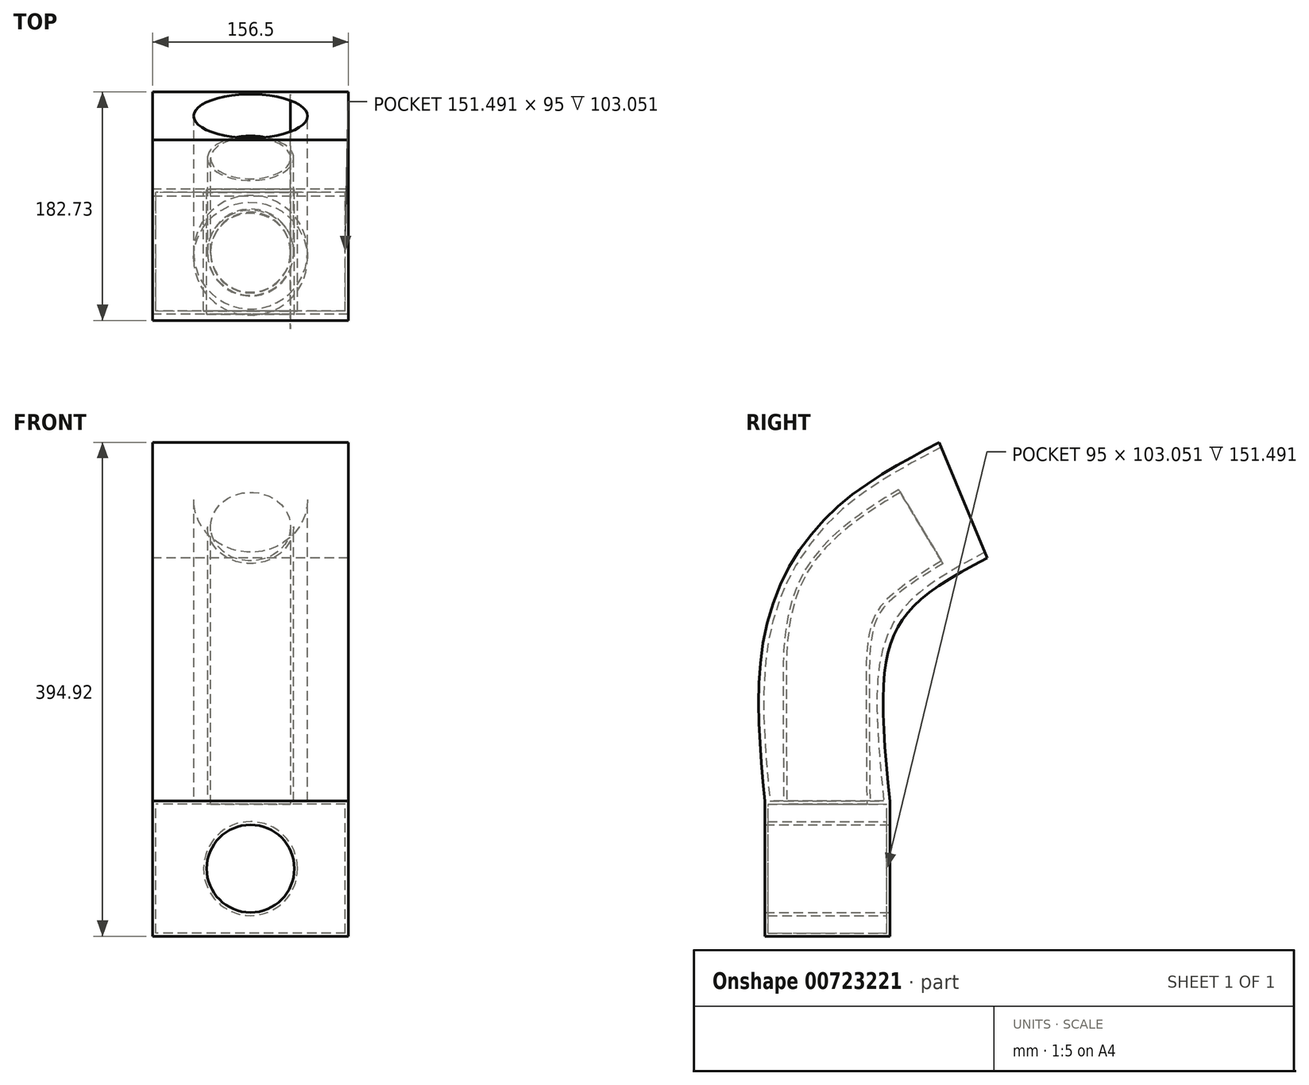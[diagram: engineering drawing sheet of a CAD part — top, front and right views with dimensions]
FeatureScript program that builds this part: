
annotation { "Feature Type Name" : "Feature", "Feature Type Description" : "" }
export const myFeature = defineFeature(function(context is Context, id is Id, definition is map)
    precondition{}
    {
        {
            var Q0;
            Q0=qCreatedBy(makeId("Front.planeOp"),FACE);
            var sketch = newSketch(context, id + "F0", { "sketchPlane" : qUnion([Q0])});
            skLineSegment(sketch, "E0.bottom", {"start": v(78.25, -54.03) * mm, "end": v(-78.25, -54.03) * mm});
            skLineSegment(sketch, "E0.top", {"start": v(78.25, 54.03) * mm, "end": v(-78.25, 54.03) * mm});
            skLineSegment(sketch, "E0.left", {"start": v(78.25, -54.03) * mm, "end": v(78.25, 54.03) * mm});
            skLineSegment(sketch, "E0.right", {"start": v(-78.25, -54.03) * mm, "end": v(-78.25, 54.03) * mm});
            skPoint(sketch, "E0.middle", {"position": v(0, 0) * mm});
            skCircle(sketch, "E1", {"center": v(0, 0) * mm, "radius": 35.05 * mm});
            skSolve(sketch);
        }
        {
            var Q0;
            Q0 = qSketchRegion(id + "F0", true);
            extrude(context, id + "F1", {"entities" : qUnion([Q0]), "depth" : 100 * mm, "offsetDistance" : 25 * mm});
        }
        {
            var Q0;
            Q0=qCreatedBy(makeId("Right.planeOp"),FACE);
            var sketch = newSketch(context, id + "F2", { "sketchPlane" : qUnion([Q0])});
            skFitSpline(sketch, "E2", {"points": [v(-49.93, 54.4) * mm, v(-50.5, 144.15) * mm, v(-38.34, 219.97) * mm, v(25.3, 273.32) * mm], "startDerivative": vector(-2.27, 260.13) * mm, "endDerivative": vector(229.88, 140.85) * mm});
            skSolve(sketch);
        }
        {
            var Q0;
            Q0=makeQuery(id+"F1.opExtrude","SWEPT_FACE",FACE,{"disambiguationData":[OSD([sQuery(id+"F0.wireOp",EDGE,"E0.top")])]});
            var sketch = newSketch(context, id + "F3", { "sketchPlane" : qUnion([Q0])});
            skCircle(sketch, "E3", {"center": v(0, -50.42) * mm, "radius": 34.47 * mm});
            skSolve(sketch);
        }
        {
            var Q0;
            Q0=makeQuery(id+"F3.imprint","IMPRINT",FACE,{"disambiguationData":[TD([[makeQuery(id+"F3.imprint","IMPRINT",EDGE,{"derivedFrom":sQuery(id+"F3.wireOp",EDGE,"E3")}),1.0]])]});
            var Q1;
            Q1=sQuery(id+"F2.wireOp",EDGE,"E2");
            sweep(context, id + "F4", {"operationType" : NewBodyOperationType.ADD, "profiles" : qUnion([Q0]), "path" : qUnion([Q1])});
        }
        {
            var Q0;
            Q0=makeQuery(id+"F4.opSweep","CAP_FACE",FACE,{"disambiguationData":[OSD([sQuery(id+"F2.wireOp",VERTEX,"E2.end"),sQuery(id+"F3.wireOp",EDGE,"E3")])],"isStart":false});
            shell(context, id + "F5", {"entities" : qUnion([Q0]), "thickness" : 2.5 * mm});
        }
        {
            var Q0;
            Q0=makeQuery(id+"F1.opExtrude","SWEPT_FACE",FACE,{"disambiguationData":[OSD([sQuery(id+"F0.wireOp",EDGE,"E0.top")])]});
            var sketch = newSketch(context, id + "F6", { "sketchPlane" : qUnion([Q0])});
            skCircle(sketch, "E4", {"center": v(0, -50.42) * mm, "radius": 45.5 * mm});
            skSolve(sketch);
        }
        {
            var Q0;
            Q0=qCreatedBy(makeId("Right.planeOp"),FACE);
            var sketch = newSketch(context, id + "F7", { "sketchPlane" : qUnion([Q0])});
            skFitSpline(sketch, "E5", {"points": [v(-50.92, 53.77) * mm, v(-52.32, 177.4) * mm, v(-14.2, 248.3) * mm, v(58.24, 295.57) * mm], "startDerivative": vector(-33.85, 348.5) * mm, "endDerivative": vector(249.2, 132.76) * mm});
            skSolve(sketch);
        }
        {
            var Q0;
            Q0=makeQuery(id+"F6.imprint","IMPRINT",FACE,{"disambiguationData":[TD([[makeQuery(id+"F6.imprint","IMPRINT",EDGE,{"derivedFrom":sQuery(id+"F6.wireOp",EDGE,"E4")}),-1.0]])]});
            var Q1;
            Q1=sQuery(id+"F7.wireOp",EDGE,"E5");
            sweep(context, id + "F8", {"operationType" : NewBodyOperationType.ADD, "profiles" : qUnion([Q0]), "path" : qUnion([Q1])});
        }
    });
